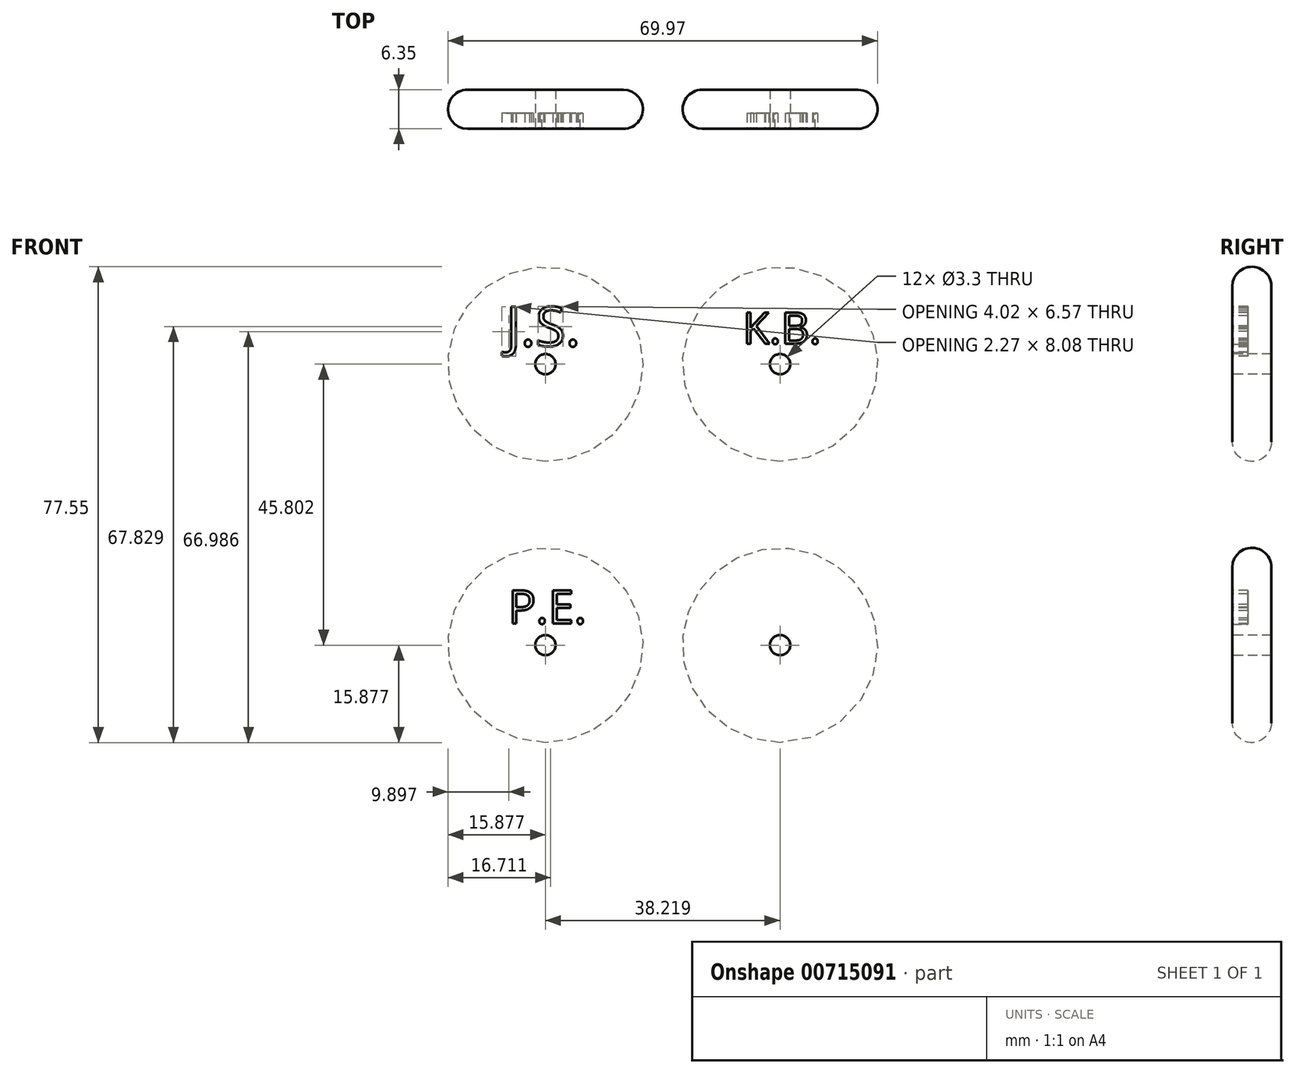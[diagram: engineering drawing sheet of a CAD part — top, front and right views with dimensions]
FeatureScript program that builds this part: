
annotation { "Feature Type Name" : "Feature", "Feature Type Description" : "" }
export const myFeature = defineFeature(function(context is Context, id is Id, definition is map)
    precondition{}
    {
        {
            var Q0;
            Q0=qCreatedBy(makeId("Front.planeOp"),FACE);
            var sketch = newSketch(context, id + "F0", { "sketchPlane" : qUnion([Q0])});
            skCircle(sketch, "E0", {"center": v(-19.76, -7.93) * mm, "radius": 15.88 * mm});
            skCircle(sketch, "E1", {"center": v(-57.98, -7.93) * mm, "radius": 15.88 * mm});
            skCircle(sketch, "E2", {"center": v(-57.98, 37.87) * mm, "radius": 15.88 * mm});
            skCircle(sketch, "E3", {"center": v(-19.76, 37.87) * mm, "radius": 15.88 * mm});
            skSolve(sketch);
        }
        {
            var Q0;
            Q0=makeQuery(id+"F0.imprint","IMPRINT",FACE,{"disambiguationData":[TD([[makeQuery(id+"F0.imprint","IMPRINT",EDGE,{"derivedFrom":sQuery(id+"F0.wireOp",EDGE,"E2")}),1.0]])]});
            var Q1;
            Q1=makeQuery(id+"F0.imprint","IMPRINT",FACE,{"disambiguationData":[TD([[makeQuery(id+"F0.imprint","IMPRINT",EDGE,{"derivedFrom":sQuery(id+"F0.wireOp",EDGE,"E1")}),1.0]])]});
            var Q2;
            Q2=makeQuery(id+"F0.imprint","IMPRINT",FACE,{"disambiguationData":[TD([[makeQuery(id+"F0.imprint","IMPRINT",EDGE,{"derivedFrom":sQuery(id+"F0.wireOp",EDGE,"E0")}),1.0]])]});
            var Q3;
            Q3=makeQuery(id+"F0.imprint","IMPRINT",FACE,{"disambiguationData":[TD([[makeQuery(id+"F0.imprint","IMPRINT",EDGE,{"derivedFrom":sQuery(id+"F0.wireOp",EDGE,"E3")}),1.0]])]});
            extrude(context, id + "F1", {"entities" : qUnion([Q0, Q1, Q2, Q3]), "depth" : 6.35 * mm, "offsetDistance" : 25.4 * mm});
        }
        {
            var Q0;
            Q0=makeQuery(id+"F1.opExtrude","CAP_FACE",FACE,{"disambiguationData":[OSD([sQuery(id+"F0.wireOp",EDGE,"E0")])],"isStart":true});
            var Q1;
            Q1=makeQuery(id+"F1.opExtrude","CAP_FACE",FACE,{"disambiguationData":[OSD([sQuery(id+"F0.wireOp",EDGE,"E3")])],"isStart":true});
            var Q2;
            Q2=makeQuery(id+"F1.opExtrude","CAP_FACE",FACE,{"disambiguationData":[OSD([sQuery(id+"F0.wireOp",EDGE,"E2")])],"isStart":true});
            var Q3;
            Q3=makeQuery(id+"F1.opExtrude","CAP_FACE",FACE,{"disambiguationData":[OSD([sQuery(id+"F0.wireOp",EDGE,"E1")])],"isStart":true});
            var Q4;
            Q4=makeQuery(id+"F1.opExtrude","CAP_FACE",FACE,{"disambiguationData":[OSD([sQuery(id+"F0.wireOp",EDGE,"E1")])],"isStart":false});
            var Q5;
            Q5=makeQuery(id+"F1.opExtrude","CAP_FACE",FACE,{"disambiguationData":[OSD([sQuery(id+"F0.wireOp",EDGE,"E2")])],"isStart":false});
            var Q6;
            Q6=makeQuery(id+"F1.opExtrude","CAP_FACE",FACE,{"disambiguationData":[OSD([sQuery(id+"F0.wireOp",EDGE,"E3")])],"isStart":false});
            var Q7;
            Q7=makeQuery(id+"F1.opExtrude","CAP_FACE",FACE,{"disambiguationData":[OSD([sQuery(id+"F0.wireOp",EDGE,"E0")])],"isStart":false});
            fillet(context, id + "F2", {"entities" : qUnion([Q0, Q1, Q2, Q3, Q4, Q5, Q6, Q7]), "radius" : 3.17 * mm, "tangentPropagation" : true, "allowEdgeOverflow" : false});
        }
        {
            var Q0;
            Q0=makeQuery(id+"F1.opExtrude","CAP_FACE",FACE,{"disambiguationData":[OSD([sQuery(id+"F0.wireOp",EDGE,"E2")])],"isStart":false});
            var sketch = newSketch(context, id + "F3", { "sketchPlane" : qUnion([Q0])});
            skCircle(sketch, "E4.0", {"center": v(-57.98, 37.87) * mm, "radius": 12.7 * mm});
            skCircle(sketch, "E5.0.0", {"center": v(-19.76, 37.87) * mm, "radius": 12.7 * mm});
            skCircle(sketch, "E6.0.0", {"center": v(-57.98, -7.93) * mm, "radius": 12.7 * mm});
            skCircle(sketch, "E7.0.0", {"center": v(-19.76, -7.93) * mm, "radius": 12.7 * mm});
            skCircle(sketch, "E8", {"center": v(-57.98, 37.87) * mm, "radius": 1.65 * mm});
            skCircle(sketch, "E9", {"center": v(-57.98, -7.93) * mm, "radius": 1.65 * mm});
            skCircle(sketch, "E10", {"center": v(-19.76, 37.87) * mm, "radius": 1.65 * mm});
            skCircle(sketch, "E11", {"center": v(-19.76, -7.93) * mm, "radius": 1.65 * mm});
            skSolve(sketch);
        }
        {
            var Q0;
            Q0=makeQuery(id+"F3.imprint","IMPRINT",FACE,{"disambiguationData":[TD([[makeQuery(id+"F3.imprint","IMPRINT",EDGE,{"derivedFrom":sQuery(id+"F3.wireOp",EDGE,"E8")}),1.0]])]});
            extrude(context, id + "F4", {"entities" : qUnion([Q0]), "operationType" : NewBodyOperationType.REMOVE, "oppositeDirection" : true, "depth" : 25.4 * mm, "offsetDistance" : 25.4 * mm});
        }
        {
            var Q0;
            Q0=makeQuery(id+"F3.imprint","IMPRINT",FACE,{"disambiguationData":[TD([[makeQuery(id+"F3.imprint","IMPRINT",EDGE,{"derivedFrom":sQuery(id+"F3.wireOp",EDGE,"E10")}),1.0]])]});
            extrude(context, id + "F5", {"entities" : qUnion([Q0]), "operationType" : NewBodyOperationType.REMOVE, "oppositeDirection" : true, "depth" : 25.4 * mm, "offsetDistance" : 25.4 * mm});
        }
        {
            var Q0;
            Q0=makeQuery(id+"F3.imprint","IMPRINT",FACE,{"disambiguationData":[TD([[makeQuery(id+"F3.imprint","IMPRINT",EDGE,{"derivedFrom":sQuery(id+"F3.wireOp",EDGE,"E9")}),1.0]])]});
            extrude(context, id + "F6", {"entities" : qUnion([Q0]), "operationType" : NewBodyOperationType.REMOVE, "oppositeDirection" : true, "depth" : 25.4 * mm, "offsetDistance" : 25.4 * mm});
        }
        {
            var Q0;
            Q0=makeQuery(id+"F3.imprint","IMPRINT",FACE,{"disambiguationData":[TD([[makeQuery(id+"F3.imprint","IMPRINT",EDGE,{"derivedFrom":sQuery(id+"F3.wireOp",EDGE,"E11")}),1.0]])]});
            extrude(context, id + "F7", {"entities" : qUnion([Q0]), "operationType" : NewBodyOperationType.REMOVE, "oppositeDirection" : true, "depth" : 25.4 * mm, "offsetDistance" : 25.4 * mm});
        }
        {
            var Q0;
            Q0=makeQuery(id+"F3.imprint","IMPRINT",FACE,{"disambiguationData":[TD([[makeQuery(id+"F3.imprint","IMPRINT",EDGE,{"derivedFrom":sQuery(id+"F3.wireOp",EDGE,"E4.0")}),1.0]])]});
            var sketch = newSketch(context, id + "F8", { "sketchPlane" : qUnion([Q0])});
            skText(sketch, "E12", { "text": "J.S.", "fontName": "OpenSans-Regular.ttf"});
            skText(sketch, "E13", { "text": "K.B.", "fontName": "OpenSans-Regular.ttf"});
            skText(sketch, "E14", { "text": "P.E.", "fontName": "OpenSans-Regular.ttf"});
            const initialGuessF8  = {"E12": [-0.0644, 0.04082, 1, 0, 0.00645], "E13": [-0.02586, 0.04122, 1, 0, 0.00512], "E14": [-0.06408, -0.0044, 1, 0, 0.00544]};
            skSetInitialGuess(sketch, initialGuessF8);
            skSolve(sketch);
        }
        {
            var Q0;
            Q0 = qSketchRegion(id + "F8", true);
            extrude(context, id + "F9", {"entities" : qUnion([Q0]), "operationType" : NewBodyOperationType.REMOVE, "oppositeDirection" : true, "depth" : 2.54 * mm, "offsetDistance" : 25.4 * mm});
        }
        {
            var Q0;
            Q0 = qSketchRegion(id + "F8", true);
            extrude(context, id + "F10", {"entities" : qUnion([Q0]), "operationType" : NewBodyOperationType.REMOVE, "oppositeDirection" : true, "depth" : 2.54 * mm, "offsetDistance" : 25.4 * mm});
        }
        {
            var Q0;
            Q0=makeQuery(id+"F3.imprint","IMPRINT",FACE,{"disambiguationData":[TD([[makeQuery(id+"F3.imprint","IMPRINT",EDGE,{"derivedFrom":sQuery(id+"F3.wireOp",EDGE,"E7.0.0")}),1.0]])]});
            var sketch = newSketch(context, id + "F11", { "sketchPlane" : qUnion([Q0])});
            skText(sketch, "E15", { "text": "VROOM", "fontName": "OpenSans-Regular.ttf"});
            const initialGuessF11  = {"E15": [0.0003, 0.00034, 1, 0, 0.00251]};
            skSetInitialGuess(sketch, initialGuessF11);
            skSolve(sketch);
        }
        {
            var Q0;
            Q0 = qSketchRegion(id + "F8", true);
            extrude(context, id + "F12", {"entities" : qUnion([Q0]), "operationType" : NewBodyOperationType.REMOVE, "oppositeDirection" : true, "depth" : 2.54 * mm, "offsetDistance" : 25.4 * mm});
        }
        {
            var Q0;
            Q0 = qSketchRegion(id + "F11", true);
            extrude(context, id + "F13", {"entities" : qUnion([Q0]), "operationType" : NewBodyOperationType.REMOVE, "oppositeDirection" : true, "depth" : 0.5 * mm, "offsetDistance" : 25.4 * mm});
        }
    });
